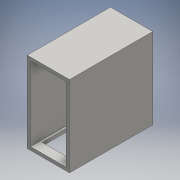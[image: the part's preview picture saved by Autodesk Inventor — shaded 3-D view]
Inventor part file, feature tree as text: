
AUTODESK INVENTOR PART (.ipt)
format: ipt  version: 2016 (Build 200138000, 138)  size: 160,768 bytes
history: native  units: mm
features: sketch x6, extrude x5
ambient origin geometry x8: Origin, YZ Plane, XZ Plane, XY Plane, X Axis, Y Axis, Z Axis, Center Point
bodies: Solid1 (feature_tree)
feature tree (11):
  extrude  "Extrusion1"  Depth=520.0mm
  extrude  "Extrusion2"  Depth=583.0mm TaperAngle=0.0deg
  extrude  "Extrusion3"  Depth=440.0mm
  sketch  "Sketch4"  dims[d7=77.0mm d8=38.0mm]
  extrude  "Extrusion4"  Depth=38.0mm
  extrude  "Extrusion5"  Depth=70.0mm
  sketch  "Sketch1"  dims[d0=250.0mm d1=520.0mm]
  sketch  "Sketch2"  dims[d2=23.0mm d3=583.0mm d4=0.0mm]
  sketch  "Sketch3"  dims[d5=220.0mm d6=440.0mm]
  sketch  "Sketch5"  dims[d9=583.0mm d10=0.0mm d11=70.0mm]
  sketch  "Sketch6"  dims[d12=80.0mm d13=430.0mm d14=143.0mm d15=583.0mm d16=0.0mm d17=47.0mm d18=583.0mm d19=0.0mm d20=16.0mm d21=170.0mm d22=45.0mm d23=16.0mm d24=170.0mm d25=45.0mm d26=10.0mm d27=0.0mm]
